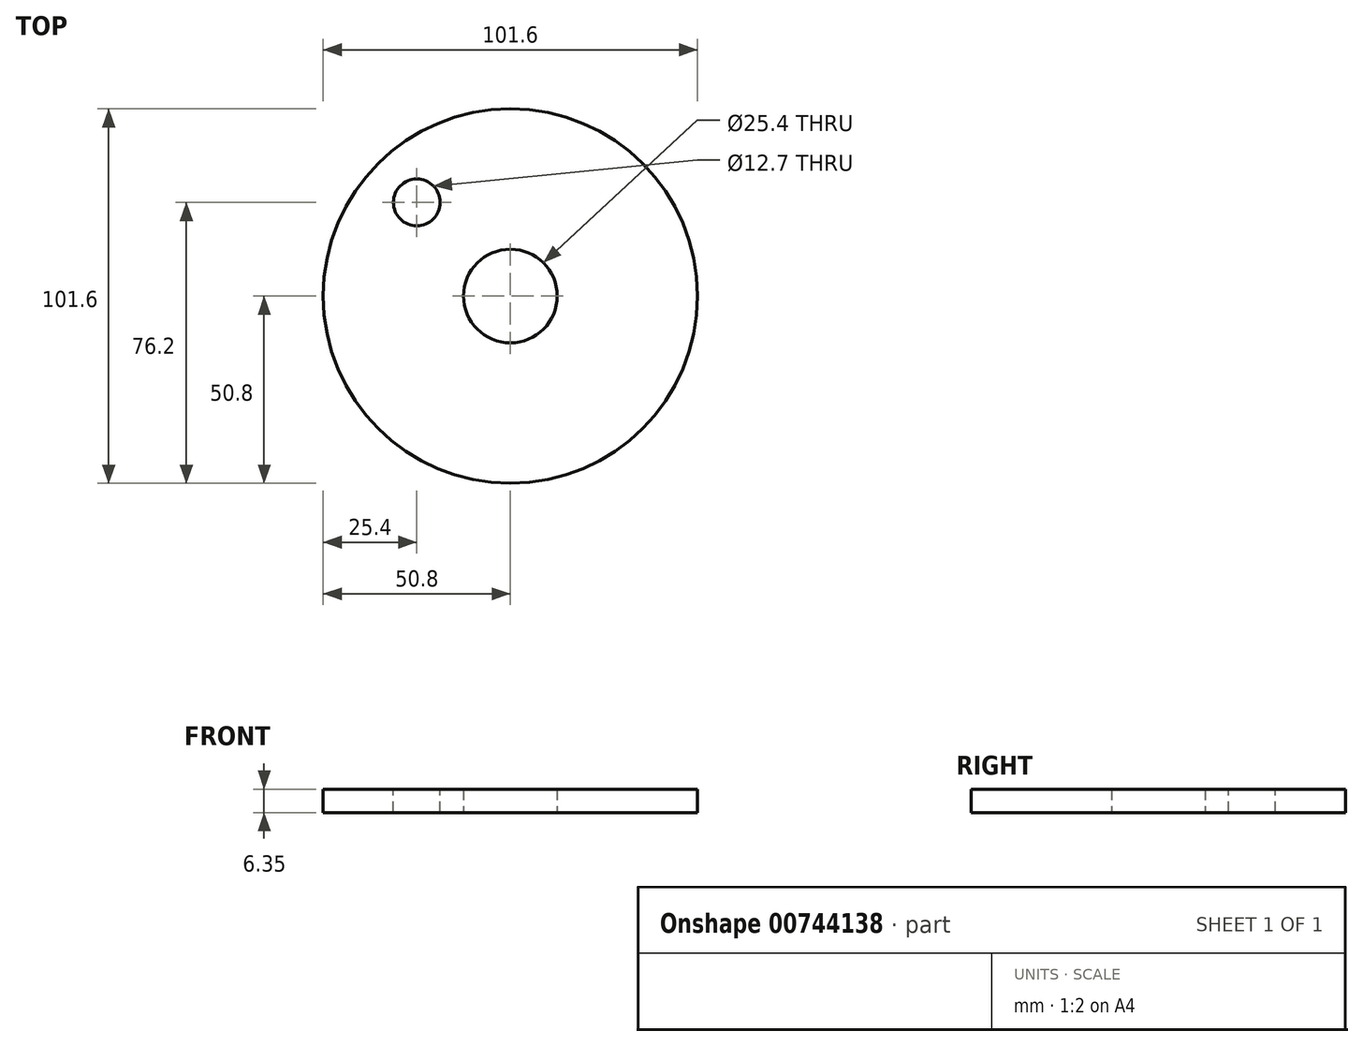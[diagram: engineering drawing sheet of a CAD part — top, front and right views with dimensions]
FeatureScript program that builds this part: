
annotation { "Feature Type Name" : "Feature", "Feature Type Description" : "" }
export const myFeature = defineFeature(function(context is Context, id is Id, definition is map)
    precondition{}
    {
        {
            var Q0;
            Q0=qCreatedBy(makeId("Top.planeOp"),FACE);
            var sketch = newSketch(context, id + "F0", { "sketchPlane" : qUnion([Q0])});
            skCircle(sketch, "E0", {"center": v(0, 0) * mm, "radius": 50.8 * mm});
            skCircle(sketch, "E1", {"center": v(0, 0) * mm, "radius": 12.7 * mm});
            skSolve(sketch);
        }
        {
            var Q0;
            Q0=makeQuery(id+"F0.imprint","IMPRINT",FACE,{"disambiguationData":[TD([[makeQuery(id+"F0.imprint","IMPRINT",EDGE,{"derivedFrom":sQuery(id+"F0.wireOp",EDGE,"E0")}),1.0]])]});
            extrude(context, id + "F1", {"entities" : qUnion([Q0]), "depth" : 6.35 * mm, "offsetDistance" : 25.4 * mm});
        }
        {
            var Q0;
            Q0=makeQuery(id+"F1.opExtrude","CAP_FACE",FACE,{"disambiguationData":[OSD([sQuery(id+"F0.wireOp",EDGE,"E0"),sQuery(id+"F0.wireOp",EDGE,"E1")])],"isStart":false});
            var sketch = newSketch(context, id + "F2", { "sketchPlane" : qUnion([Q0])});
            skCircle(sketch, "E2", {"center": v(-25.4, 25.4) * mm, "radius": 6.35 * mm});
            skLineSegment(sketch, "E3", {"start": v(0, 0) * mm, "end": v(-50.8, 0) * mm, "construction": true});
            skLineSegment(sketch, "E4", {"start": v(0, 50.8) * mm, "end": v(0, 0) * mm, "construction": true});
            skSolve(sketch);
        }
        {
            var Q0;
            Q0=makeQuery(id+"F2.imprint","IMPRINT",FACE,{"disambiguationData":[TD([[makeQuery(id+"F2.imprint","IMPRINT",EDGE,{"derivedFrom":sQuery(id+"F2.wireOp",EDGE,"E2")}),1.0]])]});
            extrude(context, id + "F3", {"entities" : qUnion([Q0]), "operationType" : NewBodyOperationType.REMOVE, "endBound" : BoundingType.THROUGH_ALL, "oppositeDirection" : true, "depth" : 25.4 * mm, "offsetDistance" : 25.4 * mm});
        }
    });
